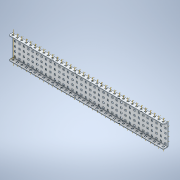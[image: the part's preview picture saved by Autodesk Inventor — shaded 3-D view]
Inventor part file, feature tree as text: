
AUTODESK INVENTOR PART (.ipt)
format: ipt  version: 2020 (Build 240168000, 168)  size: 1,916,416 bytes
history: native  units: in
note: dims shown in document units (in); Inventor stores cm internally (conversion verified against a paired STEP export)
features: other x248, plane x3, pattern_linear x3, imported_body x1
ambient origin geometry x8: Origin, YZ Plane, XZ Plane, XY Plane, X Axis, Y Axis, Z Axis, Center Point
bodies: Solid1 (feature_tree)
feature tree (255):
  plane  "Work Plane1"
  plane  "Work Plane2"
  plane  "Work Plane3"
  other  "Work Point1"
  other  "Work Point2"
  other  "Work Axis1"
  other  "Work Axis2"
  other  "Work Axis3"
  pattern_linear  "Rectangular Pattern1"  Count1=35 Spacing1=0.5in
  pattern_linear  "Rectangular Pattern2"  Count1=5 Spacing1=0.5in
  pattern_linear  "Rectangular Pattern3"  Count1=35 Spacing1=0.5in
  other  "Work Point3"
  other  "Work Axis4"
  other  "Work Axis5"
  other  "Work Axis6"
  other  "Work Axis7"
  other  "Work Axis8"
  other  "Work Axis9"
  other  "Work Axis10"
  other  "Work Axis11"
  other  "Work Axis12"
  other  "Work Axis13"
  other  "Work Axis14"
  other  "Work Axis15"
  other  "Work Axis16"
  other  "Work Axis17"
  other  "Work Axis18"
  other  "Work Axis19"
  other  "Work Axis20"
  other  "Work Axis21"
  other  "Work Axis22"
  other  "Work Axis23"
  other  "Work Axis24"
  other  "Work Axis25"
  other  "Work Axis26"
  other  "Work Axis27"
  other  "Work Axis28"
  other  "Work Axis29"
  other  "Work Axis30"
  other  "Work Axis31"
  other  "Work Axis32"
  other  "Work Axis33"
  other  "Work Axis34"
  other  "Work Axis35"
  other  "Work Axis36"
  other  "Work Axis37"
  other  "Work Axis38"
  other  "Work Axis39"
  other  "Work Axis40"
  other  "Work Axis41"
  other  "Work Axis42"
  other  "Work Axis43"
  other  "Work Axis44"
  other  "Work Axis45"
  other  "Work Axis46"
  other  "Work Axis47"
  other  "Work Axis48"
  other  "Work Axis49"
  other  "Work Axis50"
  other  "Work Axis51"
  other  "Work Axis52"
  other  "Work Axis53"
  other  "Work Axis54"
  other  "Work Axis55"
  other  "Work Axis56"
  other  "Work Axis57"
  other  "Work Axis58"
  other  "Work Axis59"
  other  "Work Axis60"
  other  "Work Axis61"
  other  "Work Axis62"
  other  "Work Axis63"
  other  "Work Axis64"
  other  "Work Axis65"
  other  "Work Axis66"
  other  "Work Axis67"
  other  "Work Axis68"
  other  "Work Axis69"
  other  "Work Axis70"
  other  "Work Axis71"
  other  "Work Axis72"
  other  "Work Axis73"
  other  "Work Axis74"
  other  "Work Axis75"
  other  "Work Axis76"
  other  "Work Axis77"
  other  "Work Axis78"
  other  "Work Axis79"
  other  "Work Axis80"
  other  "Work Axis81"
  other  "Work Axis82"
  other  "Work Axis83"
  other  "Work Axis84"
  other  "Work Axis85"
  other  "Work Axis86"
  other  "Work Axis87"
  other  "Work Axis88"
  other  "Work Axis89"
  other  "Work Axis90"
  other  "Work Axis91"
  other  "Work Axis92"
  other  "Work Axis93"
  other  "Work Axis94"
  other  "Work Axis95"
  other  "Work Axis96"
  other  "Work Axis97"
  other  "Work Axis98"
  other  "Work Axis99"
  other  "Work Axis100"
  other  "Work Axis101"
  other  "Work Axis102"
  other  "Work Axis103"
  other  "Work Axis104"
  other  "Work Axis105"
  other  "Work Axis106"
  other  "Work Axis107"
  other  "Work Axis108"
  other  "Work Axis109"
  other  "Work Axis110"
  other  "Work Axis111"
  other  "Work Axis112"
  other  "Work Axis113"
  other  "Work Axis114"
  other  "Work Axis115"
  other  "Work Axis116"
  other  "Work Axis117"
  other  "Work Axis118"
  other  "Work Axis119"
  other  "Work Axis120"
  other  "Work Axis121"
  other  "Work Axis122"
  other  "Work Axis123"
  other  "Work Axis124"
  other  "Work Axis125"
  other  "Work Axis126"
  other  "Work Axis127"
  other  "Work Axis128"
  other  "Work Axis129"
  other  "Work Axis130"
  other  "Work Axis131"
  other  "Work Axis132"
  other  "Work Axis133"
  other  "Work Axis134"
  other  "Work Axis135"
  other  "Work Axis136"
  other  "Work Axis137"
  other  "Work Axis138"
  other  "Work Axis139"
  other  "Work Axis140"
  other  "Work Axis141"
  other  "Work Axis142"
  other  "Work Axis143"
  other  "Work Axis144"
  other  "Work Axis145"
  other  "Work Axis146"
  other  "Work Axis147"
  other  "Work Axis148"
  other  "Work Axis149"
  other  "Work Axis150"
  other  "Work Axis151"
  other  "Work Axis152"
  other  "Work Axis153"
  other  "Work Axis154"
  other  "Work Axis155"
  other  "Work Axis156"
  other  "Work Axis157"
  other  "Work Axis158"
  other  "Work Axis159"
  other  "Work Axis160"
  other  "Work Axis161"
  other  "Work Axis162"
  other  "Work Axis163"
  other  "Work Axis164"
  other  "Work Axis165"
  other  "Work Axis166"
  other  "Work Axis167"
  other  "Work Axis168"
  other  "Work Axis169"
  other  "Work Axis170"
  other  "Work Axis171"
  other  "Work Axis172"
  other  "Work Axis173"
  other  "Work Axis174"
  other  "Work Axis175"
  other  "Work Axis176"
  other  "Work Axis177"
  other  "Work Axis178"
  other  "Work Axis179"
  other  "Work Axis180"
  other  "Work Axis181"
  other  "Work Axis182"
  other  "Work Axis183"
  other  "Work Axis184"
  other  "Work Axis185"
  other  "Work Axis186"
  other  "Work Axis187"
  other  "Work Axis188"
  other  "Work Axis189"
  other  "Work Axis190"
  other  "Work Axis191"
  other  "Work Axis192"
  other  "Work Axis193"
  other  "Work Axis194"
  other  "Work Axis195"
  other  "Work Axis196"
  other  "Work Axis197"
  other  "Work Axis198"
  other  "Work Axis199"
  other  "Work Axis200"
  other  "Work Axis201"
  other  "Work Axis202"
  other  "Work Axis203"
  other  "Work Axis204"
  other  "Work Axis205"
  other  "Work Axis206"
  other  "Work Axis207"
  other  "Work Axis208"
  other  "Work Axis209"
  other  "Work Axis210"
  other  "Work Axis211"
  other  "Work Axis212"
  other  "Work Axis213"
  other  "Work Axis214"
  other  "Work Axis215"
  other  "Work Axis216"
  other  "Work Axis217"
  other  "Work Axis218"
  other  "Work Axis219"
  other  "Work Axis220"
  other  "Work Axis221"
  other  "Work Axis222"
  other  "Work Axis223"
  other  "Work Axis224"
  other  "Work Axis225"
  other  "Work Axis226"
  other  "Work Axis227"
  other  "Work Axis228"
  other  "Work Axis229"
  other  "Work Axis230"
  other  "Work Axis231"
  other  "Work Axis232"
  other  "Work Axis233"
  other  "Work Axis234"
  other  "Work Axis235"
  other  "Work Axis236"
  other  "Work Axis237"
  other  "Work Axis238"
  other  "Work Axis239"
  other  "Work Axis240"
  other  "Work Axis241"
  other  "Work Axis242"
  other  "Work Axis243"
  other  "Work Axis244"
  other  "Work Axis245"
  imported_body  "Imported1"
